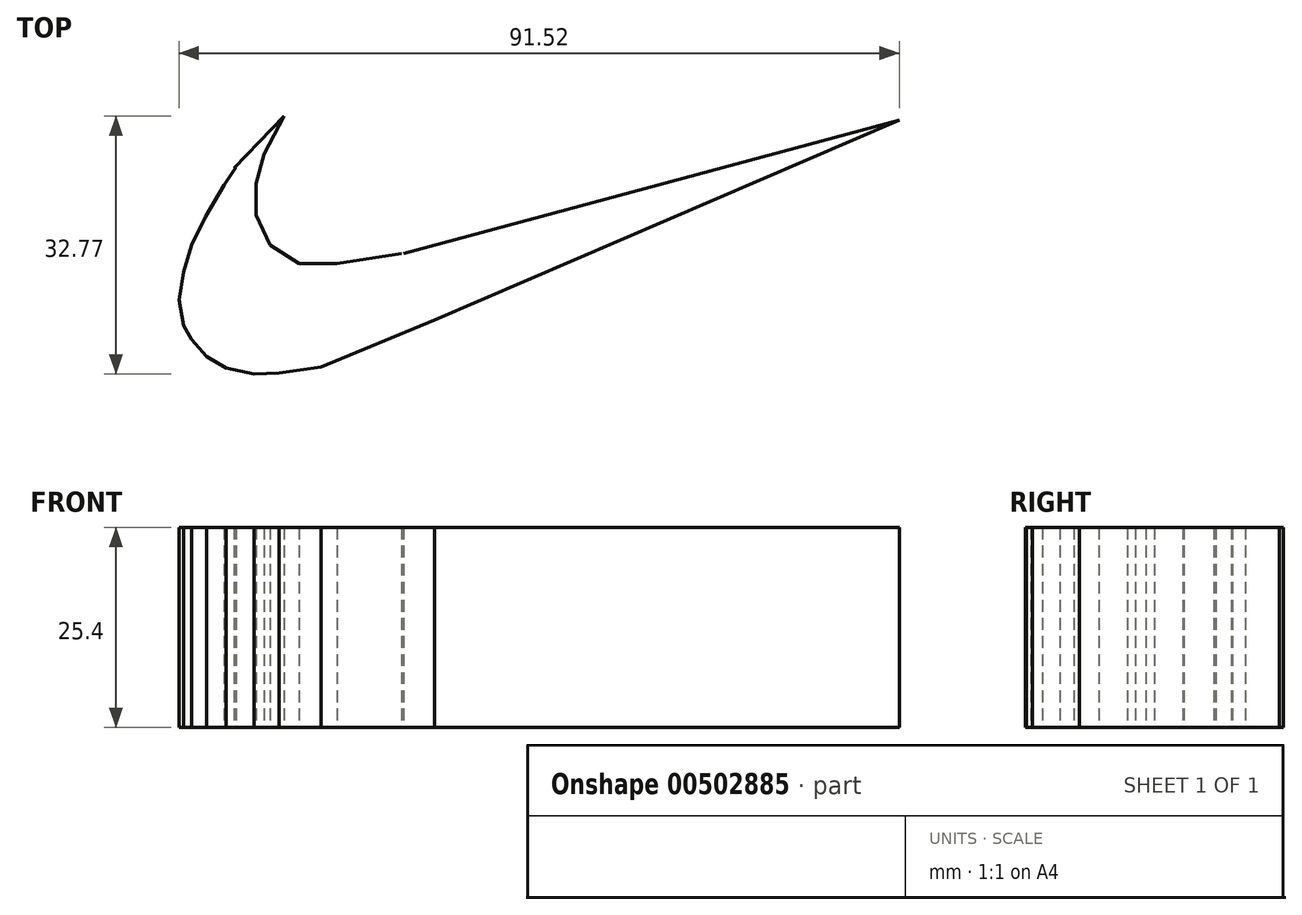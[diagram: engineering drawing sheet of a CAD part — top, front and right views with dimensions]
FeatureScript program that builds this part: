
annotation { "Feature Type Name" : "Feature", "Feature Type Description" : "" }
export const myFeature = defineFeature(function(context is Context, id is Id, definition is map)
    precondition{}
    {
        {
            var Q0;
            Q0=qCreatedBy(makeId("Top.planeOp"),FACE);
            var sketch = newSketch(context, id + "F0", { "sketchPlane" : qUnion([Q0])});
            skPoint(sketch, "E0.endSnap0", {"position": v(-33.83, -20.54) * mm});
            skLineSegment(sketch, "E1", {"start": v(50.46, -14.6) * mm, "end": v(-12.54, -31.54) * mm});
            skLineSegment(sketch, "E2", {"start": v(50.46, -14.6) * mm, "end": v(-8.62, -40) * mm});
            skLineSegment(sketch, "E3", {"start": v(-28.3, -46.7) * mm, "end": v(-23.03, -45.96) * mm});
            skLineSegment(sketch, "E4", {"start": v(-23.03, -45.96) * mm, "end": v(-8.62, -40) * mm});
            skLineSegment(sketch, "E5", {"start": v(-28.3, -46.7) * mm, "end": v(-31.53, -46.84) * mm});
            skLineSegment(sketch, "E6", {"start": v(-31.53, -46.84) * mm, "end": v(-35.05, -46.1) * mm});
            skLineSegment(sketch, "E7", {"start": v(-35.05, -46.1) * mm, "end": v(-37.54, -44.64) * mm});
            skLineSegment(sketch, "E8", {"start": v(-37.54, -44.64) * mm, "end": v(-39.45, -42.44) * mm});
            skLineSegment(sketch, "E9", {"start": v(-39.45, -42.44) * mm, "end": v(-40.48, -40.68) * mm});
            skLineSegment(sketch, "E10", {"start": v(-40.48, -40.68) * mm, "end": v(-41.06, -37.46) * mm});
            skLineSegment(sketch, "E11", {"start": v(-41.06, -37.46) * mm, "end": v(-40.44, -33.89) * mm});
            skLineSegment(sketch, "E12", {"start": v(-40.44, -33.89) * mm, "end": v(-39.45, -30.43) * mm});
            skLineSegment(sketch, "E13", {"start": v(-39.45, -30.43) * mm, "end": v(-37.69, -26.82) * mm});
            skLineSegment(sketch, "E14", {"start": v(-37.69, -26.82) * mm, "end": v(-35.34, -22.86) * mm});
            skLineSegment(sketch, "E15", {"start": v(-35.34, -22.86) * mm, "end": v(-33.83, -20.54) * mm});
            skLineSegment(sketch, "E16", {"start": v(-34.02, -20.67) * mm, "end": v(-27.72, -14.07) * mm});
            skLineSegment(sketch, "E17", {"start": v(-27.72, -14.07) * mm, "end": v(-30.21, -18.9) * mm});
            skLineSegment(sketch, "E18", {"start": v(-30.21, -18.9) * mm, "end": v(-31.28, -22.66) * mm});
            skLineSegment(sketch, "E19", {"start": v(-31.28, -22.66) * mm, "end": v(-31.28, -26.68) * mm});
            skLineSegment(sketch, "E20", {"start": v(-31.28, -26.68) * mm, "end": v(-29.48, -30.43) * mm});
            skLineSegment(sketch, "E21", {"start": v(-29.48, -30.43) * mm, "end": v(-25.81, -32.83) * mm});
            skLineSegment(sketch, "E22", {"start": v(-25.81, -32.83) * mm, "end": v(-20.97, -32.83) * mm});
            skLineSegment(sketch, "E23", {"start": v(-20.97, -32.83) * mm, "end": v(-12.76, -31.51) * mm});
            skSolve(sketch);
        }
        {
            var Q0;
            Q0=sQuery(id+"F0.wireOp",EDGE,"E23");
            var Q1;
            Q1=sQuery(id+"F0.wireOp",EDGE,"E4");
            var Q2;
            Q2=sQuery(id+"F0.wireOp",EDGE,"E1");
            var Q3;
            Q3=sQuery(id+"F0.wireOp",EDGE,"E2");
            var Q4;
            Q4=sQuery(id+"F0.wireOp",EDGE,"E6");
            var Q5;
            Q5=sQuery(id+"F0.wireOp",EDGE,"E22");
            var Q6;
            Q6=sQuery(id+"F0.wireOp",EDGE,"E21");
            var Q7;
            Q7=sQuery(id+"F0.wireOp",EDGE,"E20");
            var Q8;
            Q8=sQuery(id+"F0.wireOp",EDGE,"E10");
            var Q9;
            Q9=sQuery(id+"F0.wireOp",EDGE,"E8");
            var Q10;
            Q10=sQuery(id+"F0.wireOp",EDGE,"E3");
            var Q11;
            Q11=sQuery(id+"F0.wireOp",EDGE,"E11");
            var Q12;
            Q12=sQuery(id+"F0.wireOp",EDGE,"E5");
            var Q13;
            Q13=sQuery(id+"F0.wireOp",EDGE,"E7");
            var Q14;
            Q14=sQuery(id+"F0.wireOp",EDGE,"E17");
            var Q15;
            Q15=sQuery(id+"F0.wireOp",EDGE,"E9");
            var Q16;
            Q16=sQuery(id+"F0.wireOp",EDGE,"E14");
            var Q17;
            Q17=sQuery(id+"F0.wireOp",EDGE,"E19");
            var Q18;
            Q18=sQuery(id+"F0.wireOp",EDGE,"E16");
            var Q19;
            Q19=sQuery(id+"F0.wireOp",EDGE,"E12");
            var Q20;
            Q20=sQuery(id+"F0.wireOp",EDGE,"E13");
            var Q21;
            Q21=sQuery(id+"F0.wireOp",EDGE,"E18");
            var Q22;
            Q22=sQuery(id+"F0.wireOp",EDGE,"E15");
            extrude(context, id + "F1", {"bodyType" : ToolBodyType.SURFACE, "surfaceEntities" : qUnion([Q0, Q1, Q2, Q3, Q4, Q5, Q6, Q7, Q8, Q9, Q10, Q11, Q12, Q13, Q14, Q15, Q16, Q17, Q18, Q19, Q20, Q21, Q22]), "oppositeDirection" : true, "depth" : 25.4 * mm});
        }
    });
